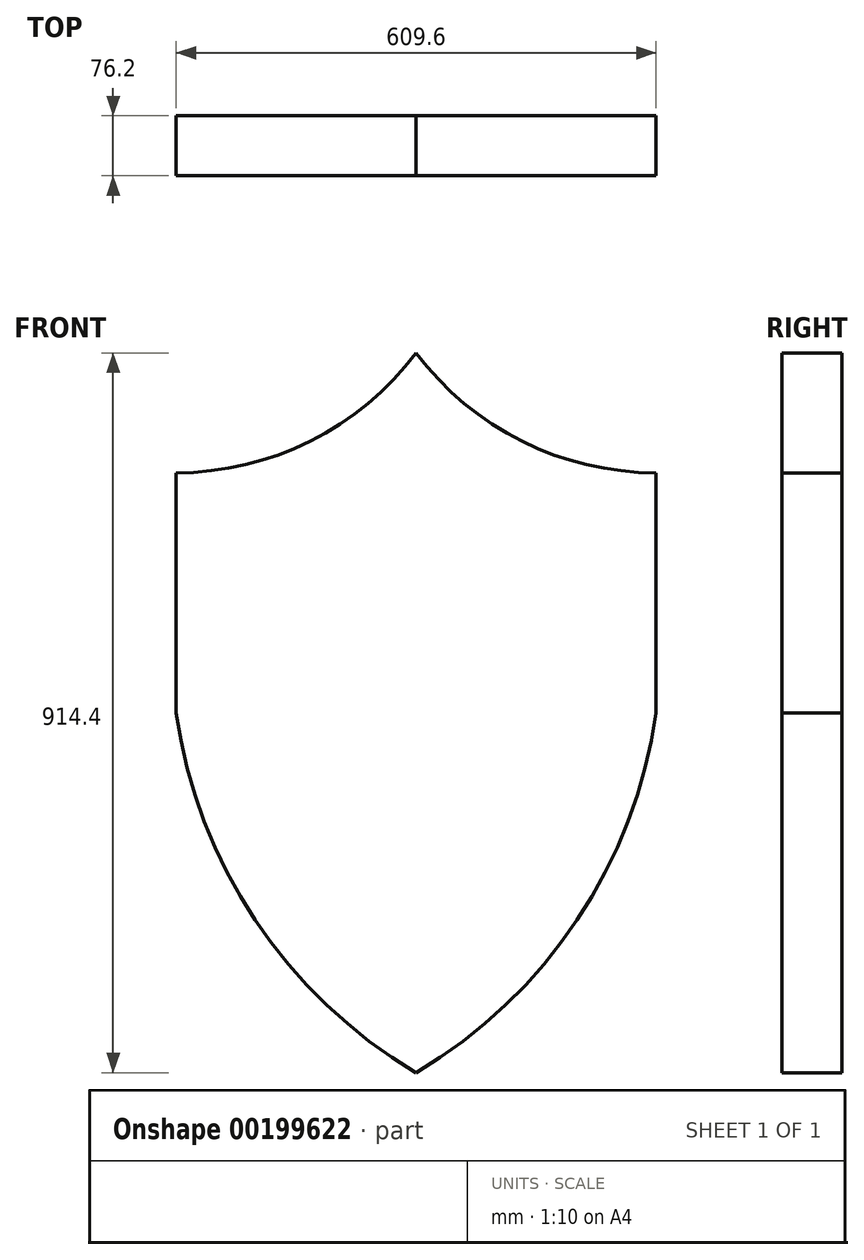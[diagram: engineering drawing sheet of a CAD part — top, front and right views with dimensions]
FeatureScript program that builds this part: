
annotation { "Feature Type Name" : "Feature", "Feature Type Description" : "" }
export const myFeature = defineFeature(function(context is Context, id is Id, definition is map)
    precondition{}
    {
        {
            var Q0;
            Q0=qCreatedBy(makeId("Front.planeOp"),FACE);
            var sketch = newSketch(context, id + "F0", { "sketchPlane" : qUnion([Q0])});
            skLineSegment(sketch, "E0.bottom", {"start": v(0, 0) * mm, "end": v(609.6, 0) * mm, "construction": true});
            skLineSegment(sketch, "E0.top", {"start": v(0, 914.4) * mm, "end": v(609.6, 914.4) * mm, "construction": true});
            skLineSegment(sketch, "E0.left", {"start": v(0, 0) * mm, "end": v(0, 914.4) * mm, "construction": true});
            skLineSegment(sketch, "E0.right", {"start": v(609.6, 0) * mm, "end": v(609.6, 914.4) * mm, "construction": true});
            skLineSegment(sketch, "E1", {"start": v(304.8, 914.4) * mm, "end": v(304.8, 0) * mm, "construction": true});
            skLineSegment(sketch, "E2", {"start": v(0, 457.2) * mm, "end": v(609.6, 457.2) * mm, "construction": true});
            skLineSegment(sketch, "E3", {"start": v(0, 762) * mm, "end": v(609.6, 762) * mm, "construction": true});
            skArc(sketch, "E4", {"start": v(0, 762) * mm, "mid": v(170.39, 802.22) * mm, "end": v(304.8, 914.4) * mm});
            skArc(sketch, "E5", {"start": v(304.8, 914.4) * mm, "mid": v(439.21, 802.22) * mm, "end": v(609.6, 762) * mm});
            skArc(sketch, "E6", {"start": v(0, 457.2) * mm, "mid": v(100.39, 193.92) * mm, "end": v(304.8, 0) * mm});
            skArc(sketch, "E7", {"start": v(304.8, 0) * mm, "mid": v(509.21, 193.92) * mm, "end": v(609.6, 457.2) * mm});
            skLineSegment(sketch, "E8", {"start": v(0, 762) * mm, "end": v(0, 457.2) * mm});
            skLineSegment(sketch, "E9", {"start": v(609.6, 762) * mm, "end": v(609.6, 457.2) * mm});
            skSolve(sketch);
        }
        {
            var Q0;
            Q0 = qSketchRegion(id + "F0", true);
            extrude(context, id + "F1", {"entities" : qUnion([Q0]), "depth" : 76.2 * mm});
        }
    });
